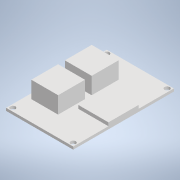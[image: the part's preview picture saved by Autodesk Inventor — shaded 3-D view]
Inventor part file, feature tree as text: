
AUTODESK INVENTOR PART (.ipt)
format: ipt  version: 2021.2 (Build 252289000, 289)  size: 137,728 bytes
history: native  units: mm
features: extrude x3, other x1, sketch x1
ambient origin geometry x8: Origin, YZ Plane, XZ Plane, XY Plane, X Axis, Y Axis, Z Axis, Center Point
bodies: Body1 (feature_tree)
feature tree (5):
  other  "Твердое тело1"
  sketch  "Эскиз1"
  extrude  "Выдавливание1"  Depth=40.0mm
  extrude  "Выдавливание2"  Depth=60.0mm
  extrude  "Выдавливание3"  Depth=16.0mm
